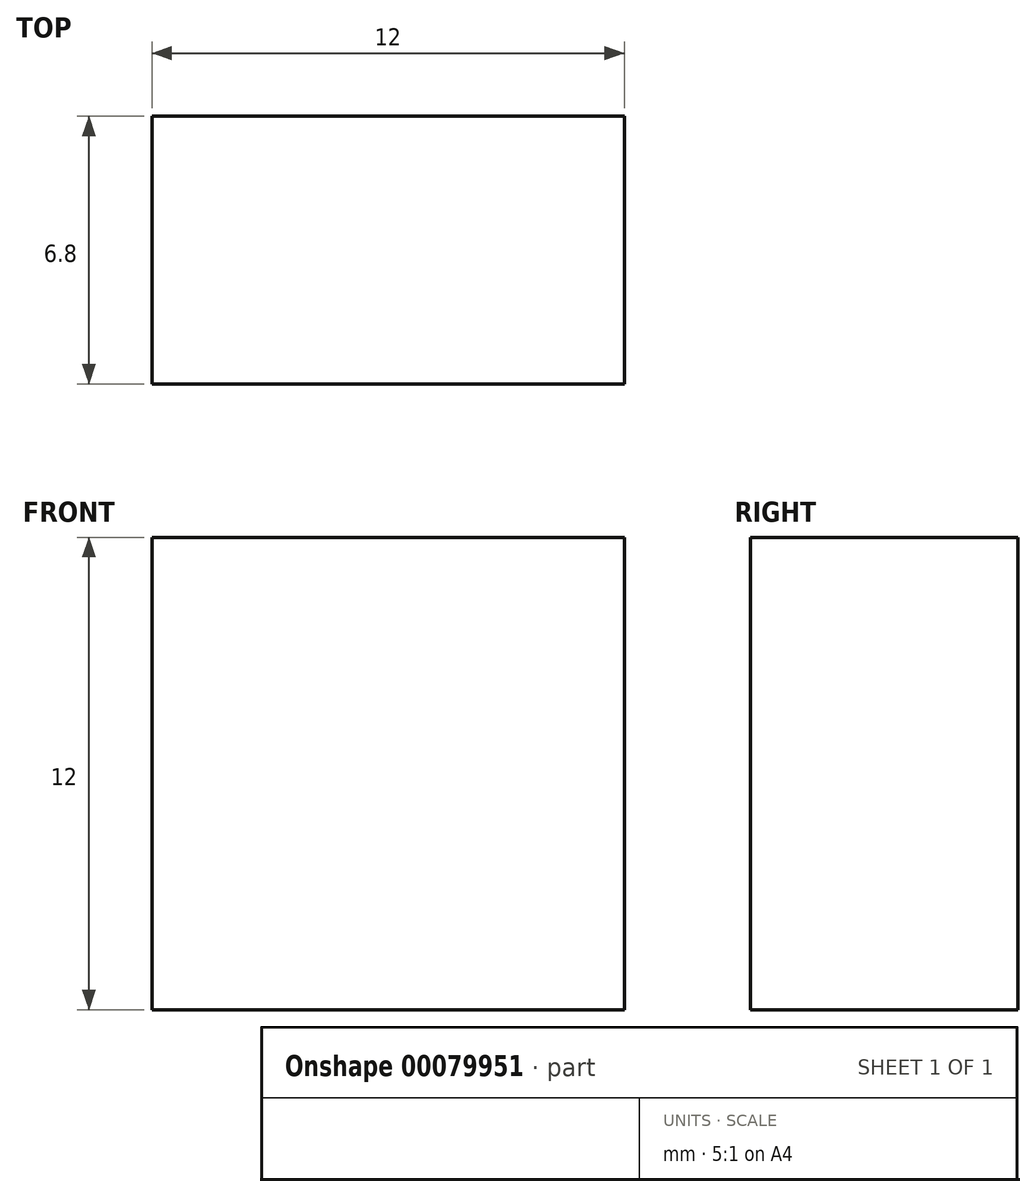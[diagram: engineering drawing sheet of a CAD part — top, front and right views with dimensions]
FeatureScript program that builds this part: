
annotation { "Feature Type Name" : "Feature", "Feature Type Description" : "" }
export const myFeature = defineFeature(function(context is Context, id is Id, definition is map)
    precondition{}
    {
        {
            var Q0;
            Q0=qCreatedBy(makeId("Front.planeOp"),FACE);
            var sketch = newSketch(context, id + "F0", { "sketchPlane" : qUnion([Q0])});
            skLineSegment(sketch, "E0.bottom", {"start": v(-6, 6) * mm, "end": v(6, 6) * mm});
            skLineSegment(sketch, "E0.top", {"start": v(-6, -6) * mm, "end": v(6, -6) * mm});
            skLineSegment(sketch, "E0.left", {"start": v(-6, 6) * mm, "end": v(-6, -6) * mm});
            skLineSegment(sketch, "E0.right", {"start": v(6, 6) * mm, "end": v(6, -6) * mm});
            skPoint(sketch, "E0.middle", {"position": v(0, 0) * mm});
            skSolve(sketch);
        }
        {
            var Q0;
            Q0=makeQuery(id+"F0.imprint","IMPRINT",FACE,{"disambiguationData":[TD([[makeQuery(id+"F0.imprint","IMPRINT",EDGE,{"derivedFrom":sQuery(id+"F0.wireOp",EDGE,"E0.bottom")}),-1.0]])]});
            extrude(context, id + "F1", {"entities" : qUnion([Q0]), "depth" : 6.8 * mm});
        }
    });
